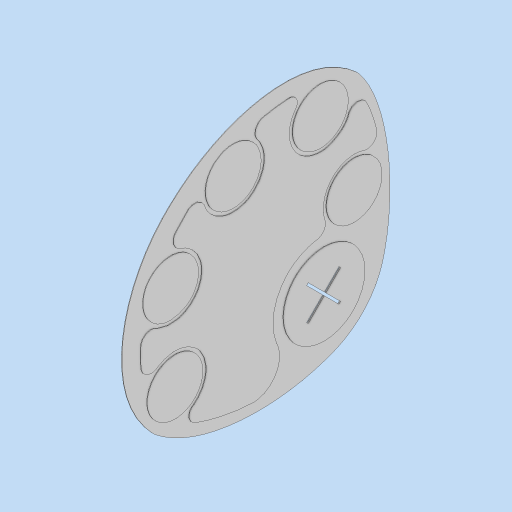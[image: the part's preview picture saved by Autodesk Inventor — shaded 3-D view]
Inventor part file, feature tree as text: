
AUTODESK INVENTOR PART (.ipt)
format: ipt  version: 2024 (Build 280153000, 153)  size: 1,290,240 bytes
history: native  units: mm
features: extrude x4, sketch x1
ambient origin geometry x8: Origin, YZ Plane, XZ Plane, XY Plane, X Axis, Y Axis, Z Axis, Center Point
bodies: Body1 (feature_tree)
feature tree (5):
  sketch  "Sketch1"  dims[d4=0.25mm d5=0.0mm d32=0.5mm d33=0.0mm d34=0.5mm d35=0.0mm d36=0.5mm d37=0.5mm d38=0.5mm d39=0.5mm d40=0.0mm d41=0.0mm d6=0.5mm d7=0.872665mm d8=0.5mm d9=0.872665mm]
  extrude  "Extrusion3"  Depth=0.5mm TaperAngle=0.0deg
  extrude  "Extrusion17"  Depth=0.5mm TaperAngle=0.0deg
  extrude  "Extrusion18"  Depth=0.5mm
  extrude  "Extrusion19"  Depth=0.5mm
